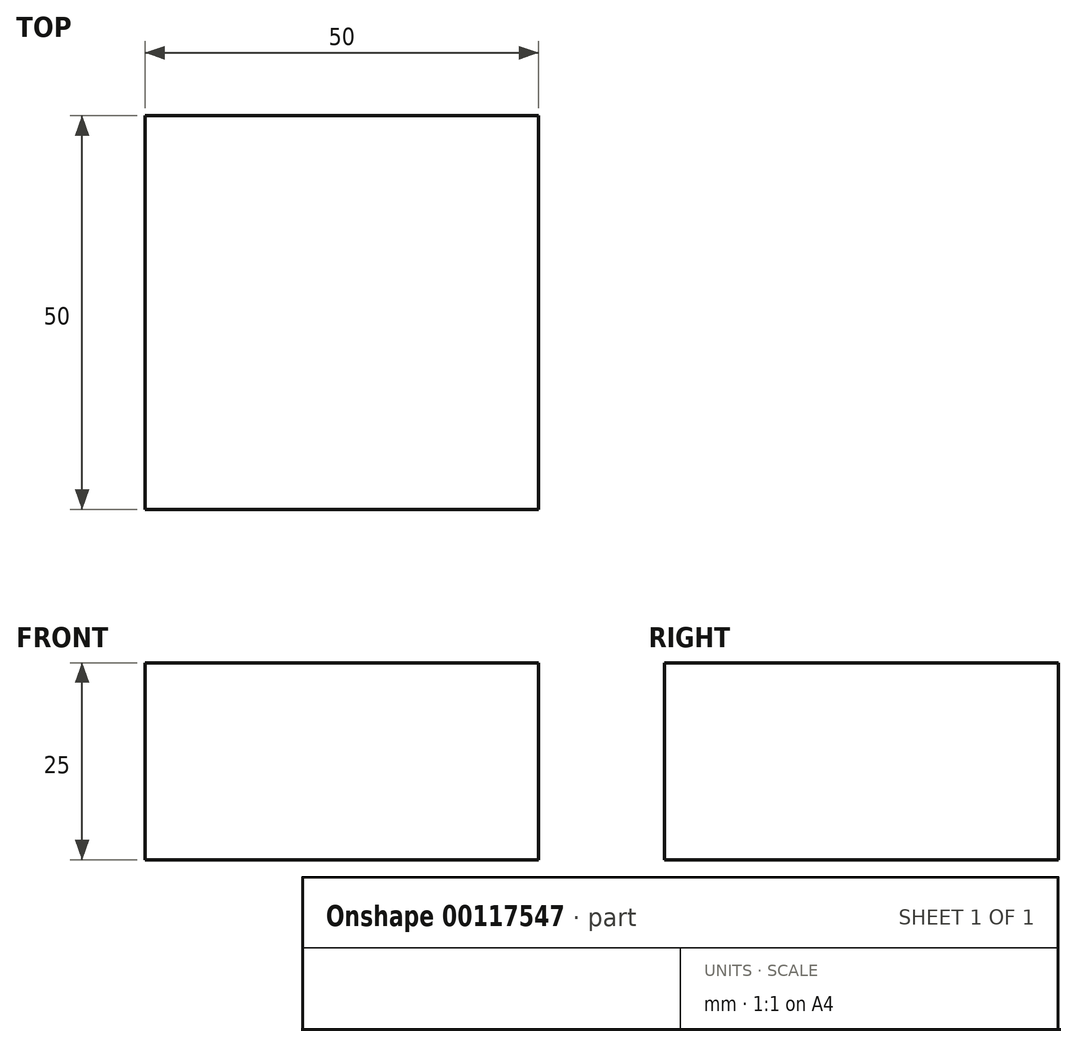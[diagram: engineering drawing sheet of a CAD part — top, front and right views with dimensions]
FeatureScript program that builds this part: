
annotation { "Feature Type Name" : "Feature", "Feature Type Description" : "" }
export const myFeature = defineFeature(function(context is Context, id is Id, definition is map)
    precondition{}
    {
        {
            var Q0;
            Q0=qCreatedBy(makeId("Top.planeOp"),FACE);
            var sketch = newSketch(context, id + "F0", { "sketchPlane" : qUnion([Q0])});
            skLineSegment(sketch, "E0.bottom", {"start": v(25, -25) * mm, "end": v(-25, -25) * mm});
            skLineSegment(sketch, "E0.top", {"start": v(25, 25) * mm, "end": v(-25, 25) * mm});
            skLineSegment(sketch, "E0.left", {"start": v(25, -25) * mm, "end": v(25, 25) * mm});
            skLineSegment(sketch, "E0.right", {"start": v(-25, -25) * mm, "end": v(-25, 25) * mm});
            skPoint(sketch, "E0.middle", {"position": v(0, 0) * mm});
            skSolve(sketch);
        }
        {
            var Q0;
            Q0=qSketchRegion(id+"F0",true);
            extrude(context, id + "F1", {"entities" : qUnion([Q0]), "depth" : 25 * mm});
        }
    });
